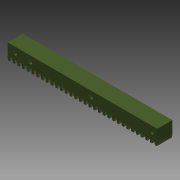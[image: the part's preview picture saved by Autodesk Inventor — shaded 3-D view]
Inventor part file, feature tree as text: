
AUTODESK INVENTOR PART (.ipt)
format: ipt  version: 2015 (Build 190159000, 159)  size: 239,104 bytes
history: native  units: in
note: dims shown in document units (in); Inventor stores cm internally (conversion verified against a paired STEP export)
features: sketch x4, extrude x3, projected_geometry x2, pattern_linear x1, hole x1
ambient origin geometry x8: Origin, YZ Plane, XZ Plane, XY Plane, X Axis, Y Axis, Z Axis, Center Point
bodies: Solid1 (feature_tree)
feature tree (11):
  extrude  "Extrusion1"  Depth=1.0in
  extrude  "Extrusion3"  Depth=0.0312in
  pattern_linear  "Rectangular Pattern2"  Spacing1=0.25in  [1 undecoded]
  hole  "Hole3"  [1 undecoded]
  extrude  "Extrusion4"  Depth=0.25in
  sketch  "Sketch1"  dims[d0=1.0in d1=1.0in]
  sketch  "Sketch2"  dims[d2=10.0in d3=0.0in d4=0.0312in]
  projected_geometry  "Projected Loop1"
  sketch  "Sketch4"  dims[d5=0.25in]
  sketch  "Sketch5"  dims[d6=0.125in d7=0.25in d8=0.0312in d9=0.25in d10=0.125in d11=0.25in d17=1.0in d18=0.0in d19=12.5984in d21=0.3125in d33=0.5in d34=0.375in d35=0.375in d44=0.5in d45=1.5in d46=4.5in d47=0.375in d48=0.375in d49=0.25in d50=0.75in d51=0.375in d52=0.25in d53=0.5635in d54=1.0in d55=0.8108in d56=0.125in d57=0.0in]
  projected_geometry  "Projected Loop3"
note: 2 required parameter values undecoded (feature->parameter linkage not recoverable at this tier; creation-order binding heuristic only, values carry confidence <= 0.55)
